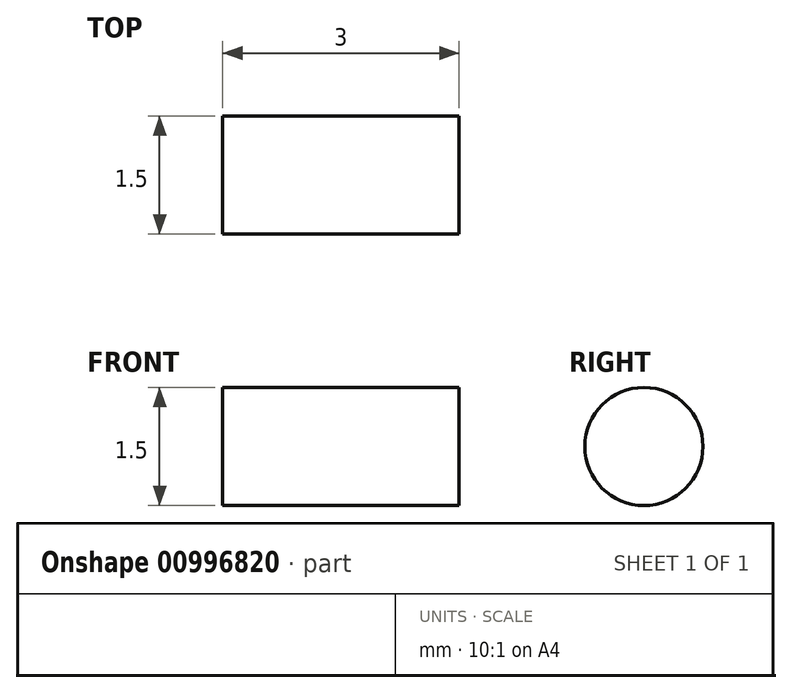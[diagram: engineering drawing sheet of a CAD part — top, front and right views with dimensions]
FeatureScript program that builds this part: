
annotation { "Feature Type Name" : "Feature", "Feature Type Description" : "" }
export const myFeature = defineFeature(function(context is Context, id is Id, definition is map)
    precondition{}
    {
        {
            var Q0;
            Q0=qCreatedBy(makeId("Right.planeOp"),FACE);
            var sketch = newSketch(context, id + "F0", { "sketchPlane" : qUnion([Q0])});
            skCircle(sketch, "E0", {"center": v(0, 0) * mm, "radius": 0.75 * mm});
            skSolve(sketch);
        }
        {
            var Q0;
            Q0 = qSketchRegion(id + "F0", true);
            extrude(context, id + "F1", {"entities" : qUnion([Q0]), "depth" : 3 * mm, "offsetDistance" : 25 * mm});
        }
    });
